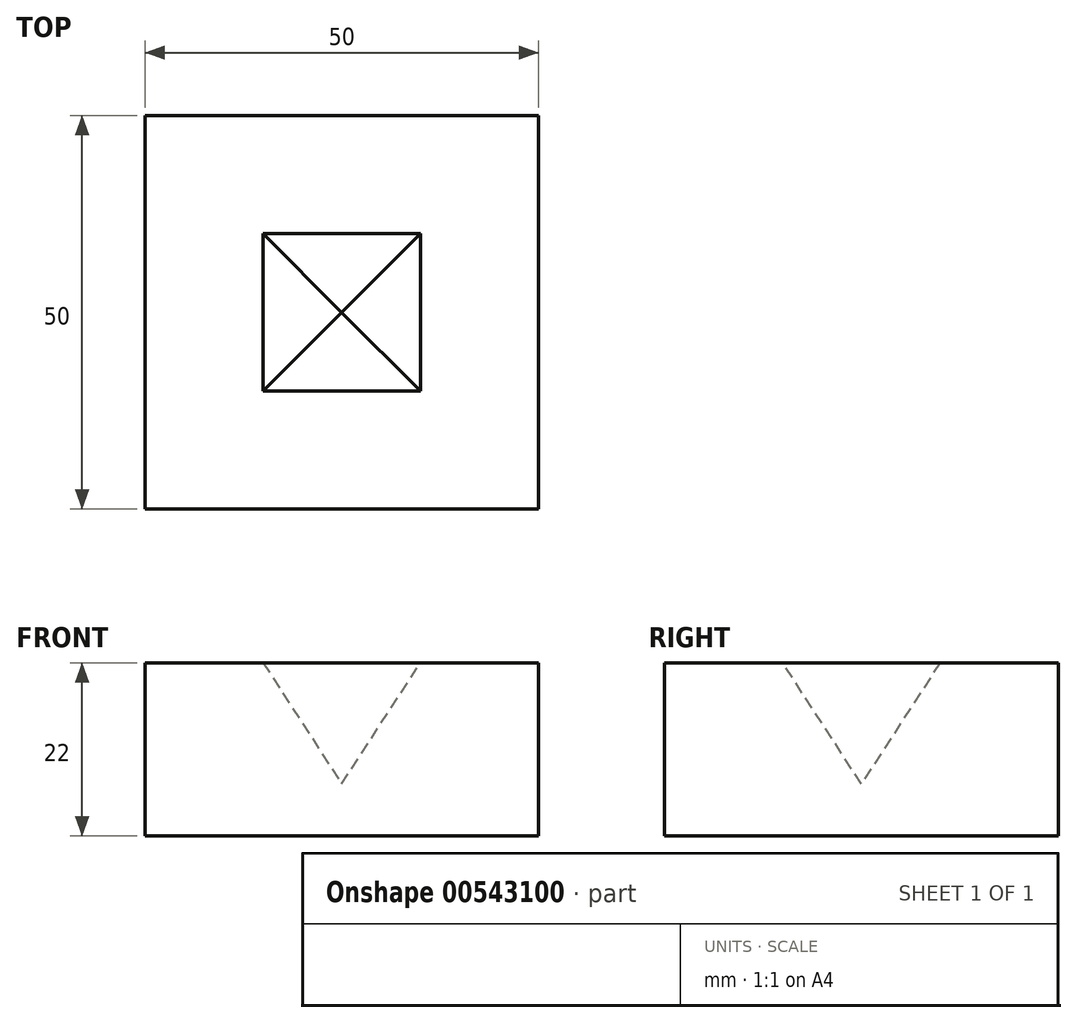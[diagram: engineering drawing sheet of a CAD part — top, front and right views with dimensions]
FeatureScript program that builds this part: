
annotation { "Feature Type Name" : "Feature", "Feature Type Description" : "" }
export const myFeature = defineFeature(function(context is Context, id is Id, definition is map)
    precondition{}
    {
        {
            var Q0;
            Q0=qCreatedBy(makeId("Top.planeOp"),FACE);
            var sketch = newSketch(context, id + "F0", { "sketchPlane" : qUnion([Q0])});
            skLineSegment(sketch, "E0.bottom", {"start": v(25, 25) * mm, "end": v(-25, 25) * mm});
            skLineSegment(sketch, "E0.top", {"start": v(25, -25) * mm, "end": v(-25, -25) * mm});
            skLineSegment(sketch, "E0.left", {"start": v(25, 25) * mm, "end": v(25, -25) * mm});
            skLineSegment(sketch, "E0.right", {"start": v(-25, 25) * mm, "end": v(-25, -25) * mm});
            skPoint(sketch, "E0.middle", {"position": v(0, 0) * mm});
            skSolve(sketch);
        }
        {
            var Q0;
            Q0=qCreatedBy(makeId("Top.planeOp"),FACE);
            var sketch = newSketch(context, id + "F1", { "sketchPlane" : qUnion([Q0])});
            skLineSegment(sketch, "E1.bottom", {"start": v(-10, 10) * mm, "end": v(10, 10) * mm});
            skLineSegment(sketch, "E1.top", {"start": v(-10, -10) * mm, "end": v(10, -10) * mm});
            skLineSegment(sketch, "E1.left", {"start": v(-10, 10) * mm, "end": v(-10, -10) * mm});
            skLineSegment(sketch, "E1.right", {"start": v(10, 10) * mm, "end": v(10, -10) * mm});
            skPoint(sketch, "E1.middle", {"position": v(0, 0) * mm});
            skSolve(sketch);
        }
        {
            var Q0;
            Q0=makeQuery(id+"F0.imprint","IMPRINT",FACE,{"disambiguationData":[TD([[makeQuery(id+"F0.imprint","IMPRINT",EDGE,{"derivedFrom":sQuery(id+"F0.wireOp",EDGE,"E0.bottom")}),1.0]])]});
            extrude(context, id + "F2", {"entities" : qUnion([Q0]), "oppositeDirection" : true, "depth" : 22 * mm, "offsetDistance" : 25 * mm});
        }
        {
            var Q0;
            Q0=makeQuery(id+"F1.imprint","IMPRINT",FACE,{"disambiguationData":[TD([[makeQuery(id+"F1.imprint","IMPRINT",EDGE,{"derivedFrom":sQuery(id+"F1.wireOp",EDGE,"E1.bottom")}),-1.0]])]});
            extrude(context, id + "F3", {"entities" : qUnion([Q0]), "operationType" : NewBodyOperationType.REMOVE, "oppositeDirection" : true, "depth" : 22.2 * mm, "offsetDistance" : 25 * mm, "hasDraft" : true, "draftAngle" : 33 * degree, "draftPullDirection" : true});
        }
    });
